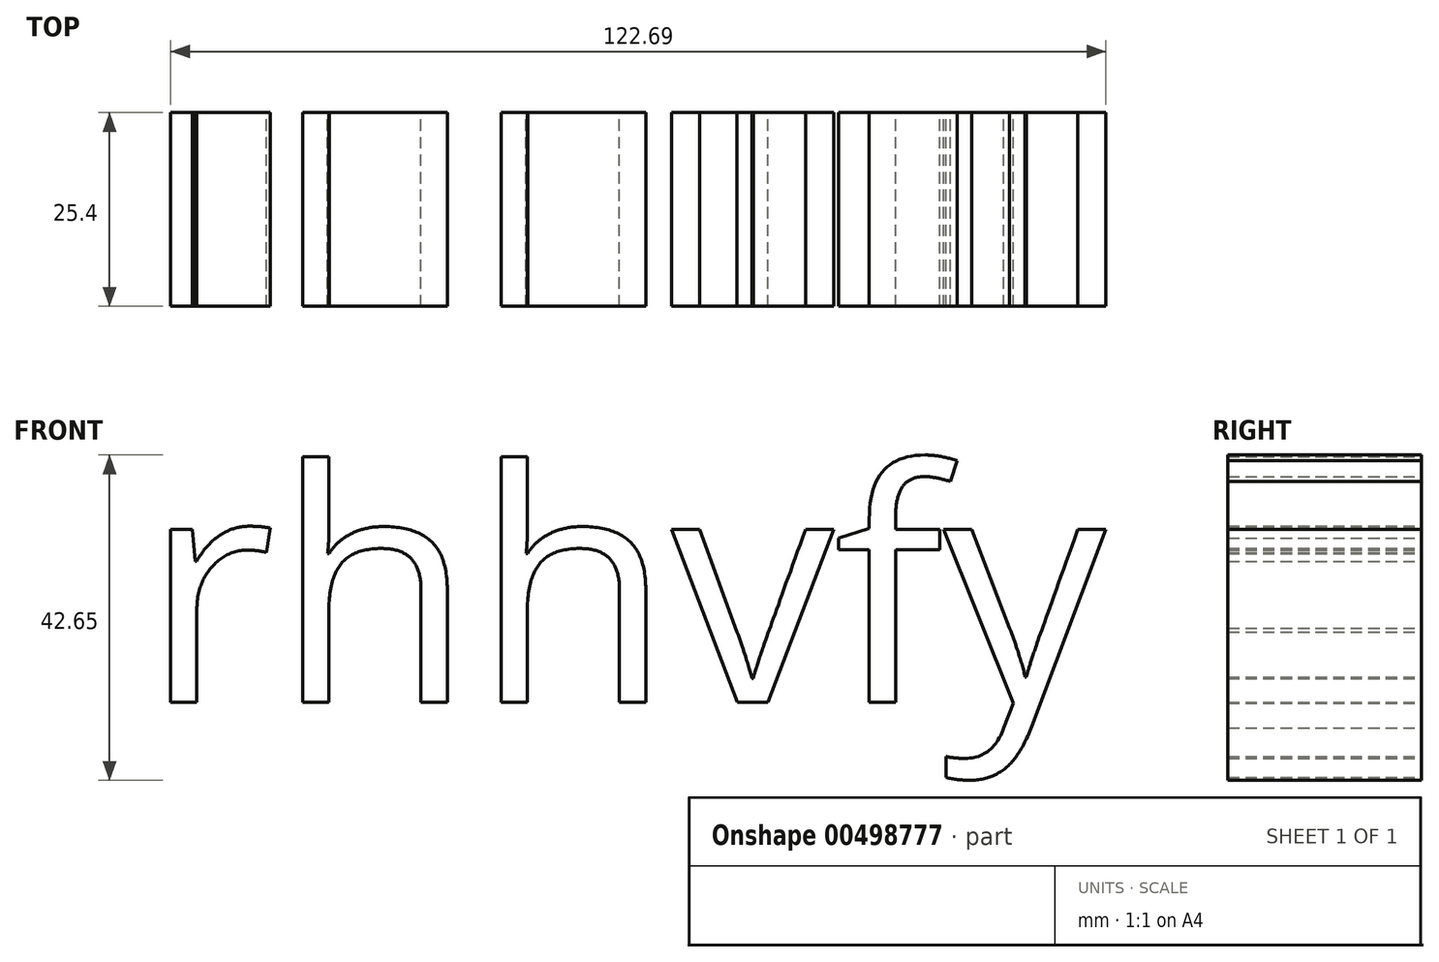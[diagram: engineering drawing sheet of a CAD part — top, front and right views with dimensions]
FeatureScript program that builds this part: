
annotation { "Feature Type Name" : "Feature", "Feature Type Description" : "" }
export const myFeature = defineFeature(function(context is Context, id is Id, definition is map)
    precondition{}
    {
        {
            var Q0;
            Q0=qCreatedBy(makeId("Front.planeOp"),FACE);
            var sketch = newSketch(context, id + "F0", { "sketchPlane" : qUnion([Q0])});
            skText(sketch, "E0", { "text": "rhhvfy", "fontName": "OpenSans-Regular.ttf"});
            const initialGuessF0  = {"E0": [-0.04777, 0.04926, 1, 0, 0.03054]};
            skSetInitialGuess(sketch, initialGuessF0);
            skSolve(sketch);
        }
        {
            var Q0;
            Q0 = qSketchRegion(id + "F0", true);
            extrude(context, id + "F1", {"entities" : qUnion([Q0]), "depth" : 25.4 * mm});
        }
    });
